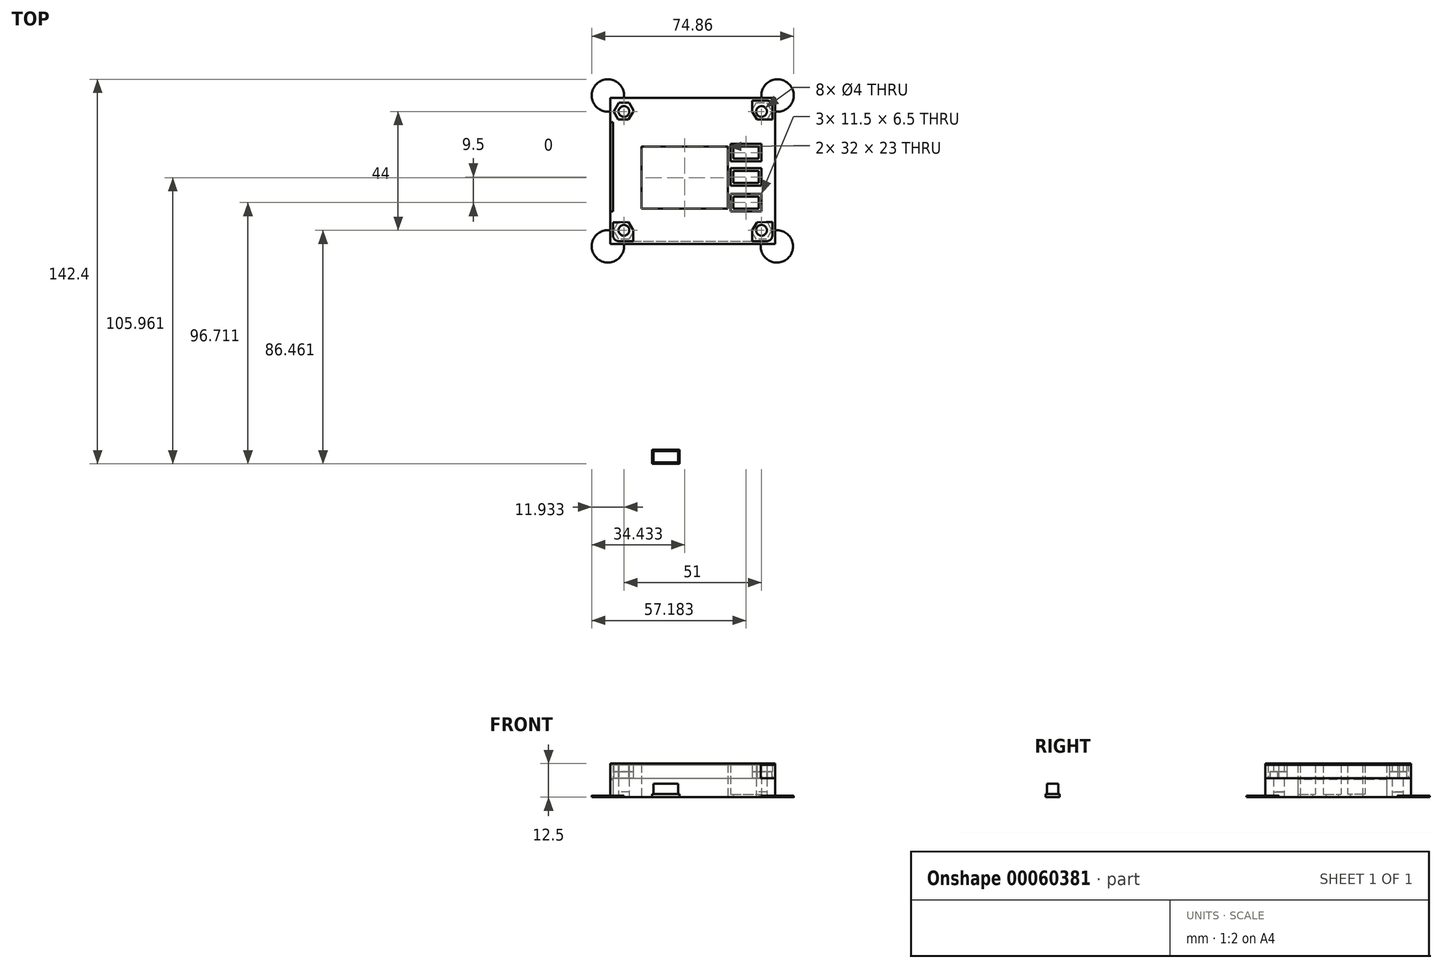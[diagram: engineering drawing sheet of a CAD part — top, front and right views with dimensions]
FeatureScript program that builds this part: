
annotation { "Feature Type Name" : "Feature", "Feature Type Description" : "" }
export const myFeature = defineFeature(function(context is Context, id is Id, definition is map)
    precondition{}
    {
        {
            var Q0;
            Q0=qCreatedBy(makeId("Top.planeOp"),FACE);
            var sketch = newSketch(context, id + "F0", { "sketchPlane" : qUnion([Q0])});
            skCircle(sketch, "E0.cCircle", {"center": v(0, 0) * mm, "radius": 3 * mm, "construction": true});
            skLineSegment(sketch, "E0.0", {"start": v(1.73, 3) * mm, "end": v(3.46, 0) * mm});
            skLineSegment(sketch, "E0.1", {"start": v(3.46, 0) * mm, "end": v(1.74, -3) * mm});
            skLineSegment(sketch, "E0.2", {"start": v(1.74, -3) * mm, "end": v(-1.73, -3) * mm});
            skLineSegment(sketch, "E0.3", {"start": v(-1.73, -3) * mm, "end": v(-3.46, 0) * mm});
            skLineSegment(sketch, "E0.4", {"start": v(-3.46, 0) * mm, "end": v(-1.74, 3) * mm});
            skLineSegment(sketch, "E0.5", {"start": v(-1.74, 3) * mm, "end": v(1.73, 3) * mm});
            skPoint(sketch, "E0.0.midPoint", {"position": v(2.6, 1.5) * mm});
            skCircle(sketch, "E1", {"center": v(0, 0) * mm, "radius": 1.5 * mm});
            skLineSegment(sketch, "E2.bottom", {"start": v(48.78, 81.41) * mm, "end": v(54.24, 81.41) * mm});
            skLineSegment(sketch, "E2.top", {"start": v(-0.76, 29.41) * mm, "end": v(6.53, 29.41) * mm});
            skLineSegment(sketch, "E2.left", {"start": v(-2.76, 79.41) * mm, "end": v(-2.76, 31.41) * mm});
            skLineSegment(sketch, "E2.right", {"start": v(56.24, 79.41) * mm, "end": v(56.24, 31.41) * mm});
            skPoint(sketch, "E3.0.midPoint", {"position": v(3.84, 78.92) * mm});
            skLineSegment(sketch, "E3.3", {"start": v(-0.48, 74.4) * mm, "end": v(-2.22, 77.4) * mm, "construction": true});
            skLineSegment(sketch, "E3.2", {"start": v(2.98, 74.41) * mm, "end": v(-0.48, 74.4) * mm});
            skLineSegment(sketch, "E3.1", {"start": v(4.7, 77.42) * mm, "end": v(2.98, 74.41) * mm});
            skLineSegment(sketch, "E3.0", {"start": v(2.97, 80.41) * mm, "end": v(4.7, 77.42) * mm, "construction": true});
            skLineSegment(sketch, "E3.4", {"start": v(-2.22, 77.4) * mm, "end": v(-0.5, 80.4) * mm, "construction": true});
            skLineSegment(sketch, "E3.5", {"start": v(-0.5, 80.4) * mm, "end": v(2.97, 80.41) * mm, "construction": true});
            skCircle(sketch, "E4", {"center": v(1.24, 77.41) * mm, "radius": 1.5 * mm, "construction": true});
            skCircle(sketch, "E3.cCircle", {"center": v(1.24, 77.41) * mm, "radius": 3 * mm, "construction": true});
            skPoint(sketch, "E5.0.midPoint", {"position": v(3.84, 34.92) * mm});
            skLineSegment(sketch, "E5.3", {"start": v(-0.48, 30.4) * mm, "end": v(-2.22, 33.4) * mm, "construction": true});
            skLineSegment(sketch, "E5.2", {"start": v(2.98, 30.41) * mm, "end": v(-0.48, 30.4) * mm, "construction": true});
            skLineSegment(sketch, "E5.1", {"start": v(4.7, 33.42) * mm, "end": v(2.98, 30.41) * mm, "construction": true});
            skLineSegment(sketch, "E5.0", {"start": v(2.97, 36.41) * mm, "end": v(4.7, 33.42) * mm});
            skLineSegment(sketch, "E5.4", {"start": v(-2.22, 33.4) * mm, "end": v(-0.5, 36.4) * mm, "construction": true});
            skLineSegment(sketch, "E5.5", {"start": v(-0.5, 36.4) * mm, "end": v(2.97, 36.41) * mm});
            skCircle(sketch, "E6", {"center": v(1.24, 33.41) * mm, "radius": 1.5 * mm, "construction": true});
            skCircle(sketch, "E5.cCircle", {"center": v(1.24, 33.41) * mm, "radius": 3 * mm, "construction": true});
            skPoint(sketch, "E7.0.midPoint", {"position": v(54.84, 78.92) * mm});
            skLineSegment(sketch, "E7.3", {"start": v(50.52, 74.4) * mm, "end": v(48.78, 77.4) * mm});
            skLineSegment(sketch, "E7.2", {"start": v(53.98, 74.41) * mm, "end": v(50.52, 74.4) * mm});
            skLineSegment(sketch, "E7.1", {"start": v(55.7, 77.42) * mm, "end": v(53.98, 74.41) * mm, "construction": true});
            skLineSegment(sketch, "E7.0", {"start": v(53.97, 80.41) * mm, "end": v(55.7, 77.42) * mm, "construction": true});
            skLineSegment(sketch, "E7.4", {"start": v(48.78, 77.4) * mm, "end": v(50.5, 80.4) * mm, "construction": true});
            skLineSegment(sketch, "E7.5", {"start": v(50.5, 80.4) * mm, "end": v(53.97, 80.41) * mm, "construction": true});
            skCircle(sketch, "E8", {"center": v(52.24, 77.41) * mm, "radius": 1.5 * mm, "construction": true});
            skCircle(sketch, "E7.cCircle", {"center": v(52.24, 77.41) * mm, "radius": 3 * mm, "construction": true});
            skPoint(sketch, "E9.0.midPoint", {"position": v(54.84, 34.92) * mm});
            skLineSegment(sketch, "E9.3", {"start": v(50.52, 30.4) * mm, "end": v(48.78, 33.4) * mm, "construction": true});
            skLineSegment(sketch, "E9.2", {"start": v(53.98, 30.41) * mm, "end": v(50.52, 30.4) * mm, "construction": true});
            skLineSegment(sketch, "E9.1", {"start": v(55.7, 33.42) * mm, "end": v(53.98, 30.41) * mm, "construction": true});
            skLineSegment(sketch, "E9.0", {"start": v(53.97, 36.41) * mm, "end": v(55.7, 33.42) * mm, "construction": true});
            skLineSegment(sketch, "E9.4", {"start": v(48.78, 33.4) * mm, "end": v(50.5, 36.4) * mm});
            skLineSegment(sketch, "E9.5", {"start": v(50.5, 36.4) * mm, "end": v(53.97, 36.41) * mm});
            skCircle(sketch, "E10", {"center": v(52.24, 33.41) * mm, "radius": 1.5 * mm, "construction": true});
            skCircle(sketch, "E9.cCircle", {"center": v(52.24, 33.41) * mm, "radius": 3 * mm, "construction": true});
            skLineSegment(sketch, "E11", {"start": v(48.78, 33.4) * mm, "end": v(48.78, 29.41) * mm});
            skLineSegment(sketch, "E12", {"start": v(53.97, 36.41) * mm, "end": v(56.24, 36.41) * mm});
            skCircle(sketch, "E13.0", {"center": v(52.24, 33.41) * mm, "radius": 2 * mm});
            skLineSegment(sketch, "E14.0", {"start": v(50.34, 30.1) * mm, "end": v(48.52, 33.25) * mm});
            skLineSegment(sketch, "E14.1", {"start": v(54.15, 30.11) * mm, "end": v(50.34, 30.1) * mm});
            skLineSegment(sketch, "E14.2", {"start": v(56.05, 33.42) * mm, "end": v(54.15, 30.11) * mm});
            skLineSegment(sketch, "E14.3", {"start": v(54.23, 36.56) * mm, "end": v(56.05, 33.42) * mm});
            skLineSegment(sketch, "E15", {"start": v(4.7, 33.42) * mm, "end": v(4.7, 29.41) * mm});
            skLineSegment(sketch, "E16", {"start": v(-0.5, 36.4) * mm, "end": v(-2.76, 36.4) * mm});
            skLineSegment(sketch, "E17", {"start": v(-0.48, 74.4) * mm, "end": v(-2.76, 74.4) * mm});
            skLineSegment(sketch, "E18", {"start": v(4.7, 77.42) * mm, "end": v(4.7, 81.41) * mm});
            skLineSegment(sketch, "E19", {"start": v(53.98, 74.41) * mm, "end": v(56.24, 74.42) * mm});
            skLineSegment(sketch, "E20", {"start": v(48.78, 77.4) * mm, "end": v(48.78, 81.41) * mm});
            skCircle(sketch, "E21.0", {"center": v(52.24, 77.41) * mm, "radius": 2 * mm});
            skCircle(sketch, "E22.0", {"center": v(1.24, 77.41) * mm, "radius": 2 * mm});
            skCircle(sketch, "E23.0", {"center": v(1.24, 33.41) * mm, "radius": 2 * mm});
            skLineSegment(sketch, "E24.0", {"start": v(3.14, 80.71) * mm, "end": v(4.97, 77.57) * mm});
            skLineSegment(sketch, "E24.1", {"start": v(-0.67, 80.7) * mm, "end": v(3.14, 80.71) * mm});
            skLineSegment(sketch, "E24.2", {"start": v(-2.57, 77.4) * mm, "end": v(-0.67, 80.7) * mm});
            skLineSegment(sketch, "E24.3", {"start": v(-0.74, 74.26) * mm, "end": v(-2.57, 77.4) * mm});
            skLineSegment(sketch, "E25.0", {"start": v(-2.57, 33.4) * mm, "end": v(-0.76, 36.56) * mm});
            skLineSegment(sketch, "E25.1", {"start": v(-0.66, 30.1) * mm, "end": v(-2.57, 33.4) * mm});
            skLineSegment(sketch, "E25.2", {"start": v(3.15, 30.11) * mm, "end": v(-0.66, 30.1) * mm});
            skLineSegment(sketch, "E25.3", {"start": v(4.97, 33.27) * mm, "end": v(3.15, 30.11) * mm});
            skLineSegment(sketch, "E26.0", {"start": v(56.05, 77.42) * mm, "end": v(44.73, 57.73) * mm});
            skLineSegment(sketch, "E26.1", {"start": v(54.14, 80.71) * mm, "end": v(56.05, 77.42) * mm});
            skLineSegment(sketch, "E26.2", {"start": v(50.33, 80.7) * mm, "end": v(54.14, 80.71) * mm});
            skLineSegment(sketch, "E26.3", {"start": v(48.52, 77.55) * mm, "end": v(50.33, 80.7) * mm});
            skPoint(sketch, "E27", {"position": v(7.74, 41.41) * mm});
            skLineSegment(sketch, "E28.bottom", {"start": v(7.74, 41.41) * mm, "end": v(39.74, 41.41) * mm});
            skLineSegment(sketch, "E28.top", {"start": v(7.74, 64.41) * mm, "end": v(39.74, 64.41) * mm});
            skLineSegment(sketch, "E28.left", {"start": v(7.74, 41.41) * mm, "end": v(7.74, 64.41) * mm});
            skLineSegment(sketch, "E28.right", {"start": v(39.74, 41.41) * mm, "end": v(39.74, 64.41) * mm});
            skPoint(sketch, "E29", {"position": v(41.74, 64.41) * mm});
            skLineSegment(sketch, "E30.bottom", {"start": v(41.74, 64.41) * mm, "end": v(51.24, 64.41) * mm});
            skLineSegment(sketch, "E30.top", {"start": v(41.74, 59.91) * mm, "end": v(51.24, 59.91) * mm});
            skLineSegment(sketch, "E30.left", {"start": v(41.74, 64.41) * mm, "end": v(41.74, 59.91) * mm});
            skLineSegment(sketch, "E30.right", {"start": v(51.24, 64.41) * mm, "end": v(51.24, 59.91) * mm});
            skLineSegment(sketch, "E31.bottom", {"start": v(41.74, 41.41) * mm, "end": v(51.24, 41.41) * mm});
            skLineSegment(sketch, "E31.top", {"start": v(41.74, 45.91) * mm, "end": v(51.24, 45.91) * mm});
            skLineSegment(sketch, "E31.left", {"start": v(41.74, 41.41) * mm, "end": v(41.74, 45.91) * mm});
            skLineSegment(sketch, "E31.right", {"start": v(51.24, 41.41) * mm, "end": v(51.24, 45.91) * mm});
            skLineSegment(sketch, "E32.bottom", {"start": v(41.74, 50.91) * mm, "end": v(51.24, 50.91) * mm});
            skLineSegment(sketch, "E32.top", {"start": v(41.74, 55.41) * mm, "end": v(51.24, 55.41) * mm});
            skLineSegment(sketch, "E32.left", {"start": v(41.74, 50.91) * mm, "end": v(41.74, 55.41) * mm});
            skLineSegment(sketch, "E32.right", {"start": v(51.24, 50.91) * mm, "end": v(51.24, 55.41) * mm});
            skLineSegment(sketch, "E33.0", {"start": v(-3.76, 82.41) * mm, "end": v(-3.76, 28.41) * mm});
            skLineSegment(sketch, "E33.1", {"start": v(-3.76, 82.41) * mm, "end": v(57.24, 82.41) * mm});
            skLineSegment(sketch, "E33.2", {"start": v(57.24, 82.41) * mm, "end": v(57.24, 28.41) * mm});
            skLineSegment(sketch, "E33.3", {"start": v(-3.76, 28.41) * mm, "end": v(57.24, 28.41) * mm});
            skPoint(sketch, "E34", {"position": v(-3.76, 73.41) * mm});
            skPoint(sketch, "E35", {"position": v(-3.76, 40.41) * mm});
            skLineSegment(sketch, "E36", {"start": v(-3.76, 73.41) * mm, "end": v(-2.76, 73.41) * mm});
            skLineSegment(sketch, "E37", {"start": v(-3.76, 40.41) * mm, "end": v(-2.76, 40.41) * mm});
            skLineSegment(sketch, "E38.bottom", {"start": v(13.09, -34.33) * mm, "end": v(22.29, -34.33) * mm});
            skLineSegment(sketch, "E38.top", {"start": v(13.09, -38.53) * mm, "end": v(22.29, -38.53) * mm});
            skLineSegment(sketch, "E38.left", {"start": v(13.09, -34.33) * mm, "end": v(13.09, -38.53) * mm});
            skLineSegment(sketch, "E38.right", {"start": v(22.29, -34.33) * mm, "end": v(22.29, -38.53) * mm});
            skLineSegment(sketch, "E39.0", {"start": v(12.09, -33.33) * mm, "end": v(23.29, -33.33) * mm});
            skLineSegment(sketch, "E39.1", {"start": v(12.09, -33.33) * mm, "end": v(12.09, -39.53) * mm});
            skLineSegment(sketch, "E39.2", {"start": v(12.09, -39.53) * mm, "end": v(23.29, -39.53) * mm});
            skLineSegment(sketch, "E39.3", {"start": v(23.29, -33.33) * mm, "end": v(23.29, -39.53) * mm});
            skLineSegment(sketch, "E40.bottom", {"start": v(12.2, -48.35) * mm, "end": v(21.4, -48.35) * mm});
            skLineSegment(sketch, "E40.top", {"start": v(12.2, -52.55) * mm, "end": v(21.4, -52.55) * mm});
            skLineSegment(sketch, "E40.left", {"start": v(12.2, -48.35) * mm, "end": v(12.2, -52.55) * mm});
            skLineSegment(sketch, "E40.right", {"start": v(21.4, -48.35) * mm, "end": v(21.4, -52.55) * mm});
            skLineSegment(sketch, "E41.0", {"start": v(11.7, -47.85) * mm, "end": v(21.9, -47.85) * mm});
            skLineSegment(sketch, "E41.1", {"start": v(11.7, -47.85) * mm, "end": v(11.7, -53.05) * mm});
            skLineSegment(sketch, "E41.2", {"start": v(11.7, -53.05) * mm, "end": v(21.9, -53.05) * mm});
            skLineSegment(sketch, "E41.3", {"start": v(21.9, -47.85) * mm, "end": v(21.9, -53.05) * mm});
            skArc(sketch, "E42", {"start": v(57.24, 77.42) * mm, "mid": v(62.4, 87.6) * mm, "end": v(52.24, 82.41) * mm});
            skArc(sketch, "E43", {"start": v(52.24, 29.41) * mm, "mid": v(61.67, 22.77) * mm, "end": v(57.24, 33.42) * mm});
            skArc(sketch, "E44", {"start": v(-3.76, 33.4) * mm, "mid": v(-8.92, 23.23) * mm, "end": v(1.24, 28.41) * mm});
            skArc(sketch, "E45", {"start": v(1.24, 82.41) * mm, "mid": v(-8.93, 87.57) * mm, "end": v(-3.76, 77.4) * mm});
            skLineSegment(sketch, "E46.0", {"start": v(40.74, 58.91) * mm, "end": v(52.24, 58.91) * mm});
            skLineSegment(sketch, "E46.1", {"start": v(40.74, 65.41) * mm, "end": v(40.74, 58.91) * mm});
            skLineSegment(sketch, "E46.2", {"start": v(40.74, 65.41) * mm, "end": v(52.24, 65.41) * mm});
            skLineSegment(sketch, "E46.3", {"start": v(52.24, 65.41) * mm, "end": v(52.24, 58.91) * mm});
            skLineSegment(sketch, "E47.0", {"start": v(40.74, 56.41) * mm, "end": v(52.24, 56.41) * mm});
            skLineSegment(sketch, "E47.1", {"start": v(40.74, 49.91) * mm, "end": v(40.74, 56.41) * mm});
            skLineSegment(sketch, "E47.2", {"start": v(40.74, 49.91) * mm, "end": v(52.24, 49.91) * mm});
            skLineSegment(sketch, "E47.3", {"start": v(52.24, 49.91) * mm, "end": v(52.24, 56.41) * mm});
            skLineSegment(sketch, "E48.0", {"start": v(40.74, 46.91) * mm, "end": v(52.24, 46.91) * mm});
            skLineSegment(sketch, "E48.1", {"start": v(40.74, 40.41) * mm, "end": v(40.74, 46.91) * mm});
            skLineSegment(sketch, "E48.2", {"start": v(40.74, 40.41) * mm, "end": v(52.24, 40.41) * mm});
            skLineSegment(sketch, "E48.3", {"start": v(52.24, 40.41) * mm, "end": v(52.24, 46.91) * mm});
            skLineSegment(sketch, "E49", {"start": v(0.74, 37.41) * mm, "end": v(52.74, 37.41) * mm, "construction": true});
            skLineSegment(sketch, "E50", {"start": v(52.74, 37.41) * mm, "end": v(52.74, 73.41) * mm, "construction": true});
            skLineSegment(sketch, "E51", {"start": v(52.74, 73.41) * mm, "end": v(0.74, 73.41) * mm, "construction": true});
            skLineSegment(sketch, "E52", {"start": v(0.74, 73.41) * mm, "end": v(0.74, 37.41) * mm, "construction": true});
            skArc(sketch, "E53", {"start": v(0.74, 55.41) * mm, "mid": v(-2.26, 52.41) * mm, "end": v(0.74, 49.41) * mm, "construction": true});
            skArc(sketch, "E54", {"start": v(52.74, 49.41) * mm, "mid": v(55.74, 52.41) * mm, "end": v(52.74, 55.41) * mm, "construction": true});
            skLineSegment(sketch, "E55", {"start": v(5.7, 81.41) * mm, "end": v(5.7, 76) * mm});
            skLineSegment(sketch, "E56", {"start": v(6.7, 75) * mm, "end": v(46.78, 75) * mm});
            skLineSegment(sketch, "E57", {"start": v(47.78, 76) * mm, "end": v(47.78, 80.41) * mm});
            skPoint(sketch, "E58.visualSharp", {"position": v(5.7, 75) * mm});
            skArc(sketch, "E58.filletArc", {"start": v(5.7, 76) * mm, "mid": v(6, 75.3) * mm, "end": v(6.7, 75) * mm});
            skPoint(sketch, "E59.visualSharp", {"position": v(-2.76, 81.41) * mm});
            skArc(sketch, "E59.filletArc", {"start": v(-0.76, 81.41) * mm, "mid": v(-2.17, 80.83) * mm, "end": v(-2.76, 79.41) * mm});
            skPoint(sketch, "E60.visualSharp", {"position": v(-2.76, 29.41) * mm});
            skArc(sketch, "E60.filletArc", {"start": v(-2.76, 31.41) * mm, "mid": v(-2.17, 30) * mm, "end": v(-0.76, 29.41) * mm});
            skPoint(sketch, "E61.visualSharp", {"position": v(56.24, 29.41) * mm});
            skArc(sketch, "E61.filletArc", {"start": v(54.24, 29.41) * mm, "mid": v(55.66, 30) * mm, "end": v(56.24, 31.41) * mm});
            skPoint(sketch, "E62.visualSharp", {"position": v(56.24, 81.41) * mm});
            skArc(sketch, "E62.filletArc", {"start": v(56.24, 79.41) * mm, "mid": v(55.66, 80.83) * mm, "end": v(54.24, 81.41) * mm});
            skPoint(sketch, "E63.visualSharp", {"position": v(47.78, 75) * mm});
            skArc(sketch, "E63.filletArc", {"start": v(46.78, 75) * mm, "mid": v(47.49, 75.3) * mm, "end": v(47.78, 76) * mm});
            skArc(sketch, "E64.filletArc", {"start": v(48.78, 81.41) * mm, "mid": v(48.07, 81.12) * mm, "end": v(47.78, 80.41) * mm});
            skLineSegment(sketch, "E65", {"start": v(6.53, 29.41) * mm, "end": v(39.2, 29.41) * mm});
            skLineSegment(sketch, "E66", {"start": v(39.2, 29.41) * mm, "end": v(54.24, 29.41) * mm});
            skSolve(sketch);
        }
        {
            var Q0;
            {var subQ12=sQuery(id+"F0.wireOp",EDGE,"E14.1");Q0=makeQuery(id+"F0.imprint","IMPRINT",FACE,{"disambiguationData":[TD([[makeQuery(id+"F0.imprint","IMPRINT",EDGE,{"derivedFrom":subQ12}),1.0]])]});}
            var Q1;
            {var subQ6=sQuery(id+"F0.wireOp",EDGE,"E9.4");Q1=makeQuery(id+"F0.imprint","IMPRINT",FACE,{"disambiguationData":[TD([[makeQuery(id+"F0.imprint","IMPRINT",EDGE,{"derivedFrom":subQ6}),-1.0]])]});}
            var Q2;
            {var subQ5=sQuery(id+"F0.wireOp",EDGE,"E25.1");Q2=makeQuery(id+"F0.imprint","IMPRINT",FACE,{"disambiguationData":[TD([[makeQuery(id+"F0.imprint","IMPRINT",EDGE,{"derivedFrom":subQ5}),1.0]])]});}
            var Q3;
            {var subQ5=sQuery(id+"F0.wireOp",EDGE,"E5.0");Q3=makeQuery(id+"F0.imprint","IMPRINT",FACE,{"disambiguationData":[TD([[makeQuery(id+"F0.imprint","IMPRINT",EDGE,{"derivedFrom":subQ5}),-1.0]])]});}
            var Q4;
            {var subQ11=sQuery(id+"F0.wireOp",EDGE,"E24.1");Q4=makeQuery(id+"F0.imprint","IMPRINT",FACE,{"disambiguationData":[TD([[makeQuery(id+"F0.imprint","IMPRINT",EDGE,{"derivedFrom":subQ11}),1.0]])]});}
            var Q5;
            {var subQ5=sQuery(id+"F0.wireOp",EDGE,"E3.2");Q5=makeQuery(id+"F0.imprint","IMPRINT",FACE,{"disambiguationData":[TD([[makeQuery(id+"F0.imprint","IMPRINT",EDGE,{"derivedFrom":subQ5}),-1.0]])]});}
            var Q6;
            {var subQ7=sQuery(id+"F0.wireOp",EDGE,"E26.1");Q6=makeQuery(id+"F0.imprint","IMPRINT",FACE,{"disambiguationData":[TD([[makeQuery(id+"F0.imprint","IMPRINT",EDGE,{"derivedFrom":subQ7}),1.0]])]});}
            var Q7;
            {var subQ1=sQuery(id+"F0.wireOp",EDGE,"E7.3");Q7=makeQuery(id+"F0.imprint","IMPRINT",FACE,{"disambiguationData":[TD([[makeQuery(id+"F0.imprint","IMPRINT",EDGE,{"derivedFrom":subQ1}),-1.0]])]});}
            extrude(context, id + "F1", {"entities" : qUnion([Q0, Q1, Q2, Q3, Q4, Q5, Q6, Q7]), "depth" : 7 * mm});
        }
        {
            var Q0;
            {var subQ12=sQuery(id+"F0.wireOp",EDGE,"E14.1");Q0=makeQuery(id+"F0.imprint","IMPRINT",FACE,{"disambiguationData":[TD([[makeQuery(id+"F0.imprint","IMPRINT",EDGE,{"derivedFrom":subQ12}),1.0]])]});}
            var Q1;
            {var subQ7=sQuery(id+"F0.wireOp",EDGE,"E26.1");Q1=makeQuery(id+"F0.imprint","IMPRINT",FACE,{"disambiguationData":[TD([[makeQuery(id+"F0.imprint","IMPRINT",EDGE,{"derivedFrom":subQ7}),1.0]])]});}
            var Q2;
            {var subQ11=sQuery(id+"F0.wireOp",EDGE,"E24.1");Q2=makeQuery(id+"F0.imprint","IMPRINT",FACE,{"disambiguationData":[TD([[makeQuery(id+"F0.imprint","IMPRINT",EDGE,{"derivedFrom":subQ11}),1.0]])]});}
            var Q3;
            {var subQ5=sQuery(id+"F0.wireOp",EDGE,"E25.1");Q3=makeQuery(id+"F0.imprint","IMPRINT",FACE,{"disambiguationData":[TD([[makeQuery(id+"F0.imprint","IMPRINT",EDGE,{"derivedFrom":subQ5}),1.0]])]});}
            extrude(context, id + "F2", {"entities" : qUnion([Q0, Q1, Q2, Q3]), "endBound" : BoundingType.UP_TO_NEXT, "depth" : 25 * mm});
        }
        {
            var Q0;
            Q0=makeQuery(id+"F2.opExtrude","CAP_FACE",FACE,{"disambiguationData":[OSD([sQuery(id+"F0.wireOp",EDGE,"E2.top"),sQuery(id+"F0.wireOp",EDGE,"E2.right"),sQuery(id+"F0.wireOp",EDGE,"E9.4"),sQuery(id+"F0.wireOp",EDGE,"E9.5"),sQuery(id+"F0.wireOp",EDGE,"E11"),sQuery(id+"F0.wireOp",EDGE,"E12"),sQuery(id+"F0.wireOp",EDGE,"E13.0")])],"isStart":false});
            var Q1;
            Q1=makeQuery(id+"F2.opExtrude","CAP_FACE",FACE,{"disambiguationData":[OSD([sQuery(id+"F0.wireOp",EDGE,"E2.top"),sQuery(id+"F0.wireOp",EDGE,"E2.left"),sQuery(id+"F0.wireOp",EDGE,"E5.0"),sQuery(id+"F0.wireOp",EDGE,"E5.5"),sQuery(id+"F0.wireOp",EDGE,"E15"),sQuery(id+"F0.wireOp",EDGE,"E16"),sQuery(id+"F0.wireOp",EDGE,"E23.0")])],"isStart":false});
            var Q2;
            Q2=makeQuery(id+"F2.opExtrude","CAP_FACE",FACE,{"disambiguationData":[OSD([sQuery(id+"F0.wireOp",EDGE,"E2.bottom"),sQuery(id+"F0.wireOp",EDGE,"E2.left"),sQuery(id+"F0.wireOp",EDGE,"E3.2"),sQuery(id+"F0.wireOp",EDGE,"E3.1"),sQuery(id+"F0.wireOp",EDGE,"E17"),sQuery(id+"F0.wireOp",EDGE,"E18"),sQuery(id+"F0.wireOp",EDGE,"E22.0")])],"isStart":false});
            var Q3;
            Q3=makeQuery(id+"F2.opExtrude","CAP_FACE",FACE,{"disambiguationData":[OSD([sQuery(id+"F0.wireOp",EDGE,"E2.bottom"),sQuery(id+"F0.wireOp",EDGE,"E2.right"),sQuery(id+"F0.wireOp",EDGE,"E7.3"),sQuery(id+"F0.wireOp",EDGE,"E7.2"),sQuery(id+"F0.wireOp",EDGE,"E19"),sQuery(id+"F0.wireOp",EDGE,"E20"),sQuery(id+"F0.wireOp",EDGE,"E21.0")])],"isStart":false});
            extrude(context, id + "F3", {"entities" : qUnion([Q0, Q1, Q2, Q3]), "depth" : 2.5 * mm});
        }
        {
            var Q0;
            Q0=makeQuery(id+"F1.opExtrude","CAP_FACE",FACE,{"disambiguationData":[OSD([sQuery(id+"F0.wireOp",EDGE,"E2.top"),sQuery(id+"F0.wireOp",EDGE,"E2.right"),sQuery(id+"F0.wireOp",EDGE,"E9.4"),sQuery(id+"F0.wireOp",EDGE,"E9.5"),sQuery(id+"F0.wireOp",EDGE,"E11"),sQuery(id+"F0.wireOp",EDGE,"E12"),sQuery(id+"F0.wireOp",EDGE,"E13.0")])],"isStart":false});
            var Q1;
            Q1=makeQuery(id+"F1.opExtrude","CAP_FACE",FACE,{"disambiguationData":[OSD([sQuery(id+"F0.wireOp",EDGE,"E2.top"),sQuery(id+"F0.wireOp",EDGE,"E2.left"),sQuery(id+"F0.wireOp",EDGE,"E5.0"),sQuery(id+"F0.wireOp",EDGE,"E5.5"),sQuery(id+"F0.wireOp",EDGE,"E15"),sQuery(id+"F0.wireOp",EDGE,"E16"),sQuery(id+"F0.wireOp",EDGE,"E23.0")])],"isStart":false});
            var Q2;
            Q2=makeQuery(id+"F1.opExtrude","CAP_FACE",FACE,{"disambiguationData":[OSD([sQuery(id+"F0.wireOp",EDGE,"E2.bottom"),sQuery(id+"F0.wireOp",EDGE,"E2.left"),sQuery(id+"F0.wireOp",EDGE,"E3.2"),sQuery(id+"F0.wireOp",EDGE,"E3.1"),sQuery(id+"F0.wireOp",EDGE,"E17"),sQuery(id+"F0.wireOp",EDGE,"E18"),sQuery(id+"F0.wireOp",EDGE,"E22.0")])],"isStart":false});
            var Q3;
            Q3=makeQuery(id+"F1.opExtrude","CAP_FACE",FACE,{"disambiguationData":[OSD([sQuery(id+"F0.wireOp",EDGE,"E2.bottom"),sQuery(id+"F0.wireOp",EDGE,"E2.right"),sQuery(id+"F0.wireOp",EDGE,"E7.3"),sQuery(id+"F0.wireOp",EDGE,"E7.2"),sQuery(id+"F0.wireOp",EDGE,"E19"),sQuery(id+"F0.wireOp",EDGE,"E20"),sQuery(id+"F0.wireOp",EDGE,"E21.0")])],"isStart":false});
            extrude(context, id + "F4", {"entities" : qUnion([Q0, Q1, Q2, Q3]), "operationType" : NewBodyOperationType.ADD, "depth" : 5 * mm, "hasSecondDirection" : true, "secondDirectionOppositeDirection" : false, "secondDirectionDepth" : 2.5 * mm});
        }
        {
            var Q0;
            {var subQ14=sQuery(id+"F0.wireOp",EDGE,"E3.2");Q0=makeQuery(id+"F0.imprint","IMPRINT",FACE,{"disambiguationData":[TD([[makeQuery(id+"F0.imprint","IMPRINT",EDGE,{"derivedFrom":subQ14}),1.0]])]});}
            var Q1;
            Q1=makeQuery(id+"F0.imprint","IMPRINT",FACE,{"disambiguationData":[TD([[makeQuery(id+"F0.imprint","IMPRINT",EDGE,{"derivedFrom":sQuery(id+"F0.wireOp",EDGE,"E22.0")}),1.0]])]});
            var Q2;
            Q2=makeQuery(id+"F0.imprint","IMPRINT",FACE,{"disambiguationData":[TD([[makeQuery(id+"F0.imprint","IMPRINT",EDGE,{"derivedFrom":sQuery(id+"F0.wireOp",EDGE,"E21.0")}),1.0]])]});
            var Q3;
            Q3=makeQuery(id+"F0.imprint","IMPRINT",FACE,{"disambiguationData":[TD([[makeQuery(id+"F0.imprint","IMPRINT",EDGE,{"derivedFrom":sQuery(id+"F0.wireOp",EDGE,"E13.0")}),1.0]])]});
            var Q4;
            Q4=makeQuery(id+"F0.imprint","IMPRINT",FACE,{"disambiguationData":[TD([[makeQuery(id+"F0.imprint","IMPRINT",EDGE,{"derivedFrom":sQuery(id+"F0.wireOp",EDGE,"E23.0")}),1.0]])]});
            extrude(context, id + "F5", {"entities" : qUnion([Q0, Q1, Q2, Q3, Q4]), "depth" : 2 * mm});
        }
        {
            var Q0;
            Q0=makeQuery(id+"F0.imprint","IMPRINT",FACE,{"disambiguationData":[TD([[makeQuery(id+"F0.imprint","IMPRINT",EDGE,{"derivedFrom":sQuery(id+"F0.wireOp",EDGE,"E30.bottom")}),1.0]])]});
            var Q1;
            Q1=makeQuery(id+"F0.imprint","IMPRINT",FACE,{"disambiguationData":[TD([[makeQuery(id+"F0.imprint","IMPRINT",EDGE,{"derivedFrom":sQuery(id+"F0.wireOp",EDGE,"E32.bottom")}),-1.0]])]});
            var Q2;
            Q2=makeQuery(id+"F0.imprint","IMPRINT",FACE,{"disambiguationData":[TD([[makeQuery(id+"F0.imprint","IMPRINT",EDGE,{"derivedFrom":sQuery(id+"F0.wireOp",EDGE,"E31.bottom")}),-1.0]])]});
            extrude(context, id + "F6", {"entities" : qUnion([Q0, Q1, Q2]), "operationType" : NewBodyOperationType.ADD, "depth" : 1 * mm});
        }
        {
            var Q0;
            {var subQ18=sQuery(id+"F0.wireOp",EDGE,"E33.1");Q0=makeQuery(id+"F0.imprint","IMPRINT",FACE,{"disambiguationData":[TD([[makeQuery(id+"F0.imprint","IMPRINT",EDGE,{"derivedFrom":subQ18}),-1.0]])]});}
            var Q1;
            {var subQ0=sQuery(id+"F0.wireOp",EDGE,"E37");Q1=makeQuery(id+"F0.imprint","IMPRINT",FACE,{"disambiguationData":[TD([[makeQuery(id+"F0.imprint","IMPRINT",EDGE,{"derivedFrom":subQ0}),-1.0]])]});}
            extrude(context, id + "F7", {"entities" : qUnion([Q0, Q1]), "depth" : 12.5 * mm});
        }
        {
            var Q0;
            {var subQ0=sQuery(id+"F0.wireOp",EDGE,"E36");Q0=makeQuery(id+"F0.imprint","IMPRINT",FACE,{"disambiguationData":[TD([[makeQuery(id+"F0.imprint","IMPRINT",EDGE,{"derivedFrom":subQ0}),-1.0]])]});}
            extrude(context, id + "F8", {"entities" : qUnion([Q0]), "depth" : 6.5 * mm});
        }
        {
            var Q0;
            Q0=makeQuery(id+"F0.imprint","IMPRINT",FACE,{"disambiguationData":[TD([[makeQuery(id+"F0.imprint","IMPRINT",EDGE,{"derivedFrom":sQuery(id+"F0.wireOp",EDGE,"E40.bottom")}),1.0]])]});
            extrude(context, id + "F9", {"entities" : qUnion([Q0]), "depth" : 1.2 * mm});
        }
        {
            var Q0;
            Q0=makeQuery(id+"F0.imprint","IMPRINT",FACE,{"disambiguationData":[TD([[makeQuery(id+"F0.imprint","IMPRINT",EDGE,{"derivedFrom":sQuery(id+"F0.wireOp",EDGE,"E40.bottom")}),-1.0]])]});
            extrude(context, id + "F10", {"entities" : qUnion([Q0]), "operationType" : NewBodyOperationType.ADD, "depth" : 5 * mm});
        }
        {
            var Q0;
            {var subQ3=sQuery(id+"F0.wireOp",EDGE,"E44");Q0=makeQuery(id+"F0.imprint","IMPRINT",FACE,{"disambiguationData":[TD([[makeQuery(id+"F0.imprint","IMPRINT",EDGE,{"derivedFrom":subQ3}),1.0]])]});}
            var Q1;
            {var subQ3=sQuery(id+"F0.wireOp",EDGE,"E45");Q1=makeQuery(id+"F0.imprint","IMPRINT",FACE,{"disambiguationData":[TD([[makeQuery(id+"F0.imprint","IMPRINT",EDGE,{"derivedFrom":subQ3}),1.0]])]});}
            var Q2;
            {var subQ3=sQuery(id+"F0.wireOp",EDGE,"E42");Q2=makeQuery(id+"F0.imprint","IMPRINT",FACE,{"disambiguationData":[TD([[makeQuery(id+"F0.imprint","IMPRINT",EDGE,{"derivedFrom":subQ3}),1.0]])]});}
            var Q3;
            {var subQ0=sQuery(id+"F0.wireOp",EDGE,"E33.3");var subQ1=sQuery(id+"F0.wireOp",EDGE,"E33.2");var subQ2=makeQuery(id+"F0.imprint","INTERSECT",VERTEX,{"derivedFrom":[subQ1,subQ0]});Q3=makeQuery(id+"F0.imprint","IMPRINT",FACE,{"disambiguationData":[TD([[makeQuery(id+"F0.imprint","IMPRINT",EDGE,{"disambiguationData":[TD([[subQ2,1.0]])],"derivedFrom":subQ1}),1.0]])]});}
            extrude(context, id + "F11", {"entities" : qUnion([Q0, Q1, Q2, Q3]), "operationType" : NewBodyOperationType.ADD, "depth" : 0.5 * mm});
        }
    });
